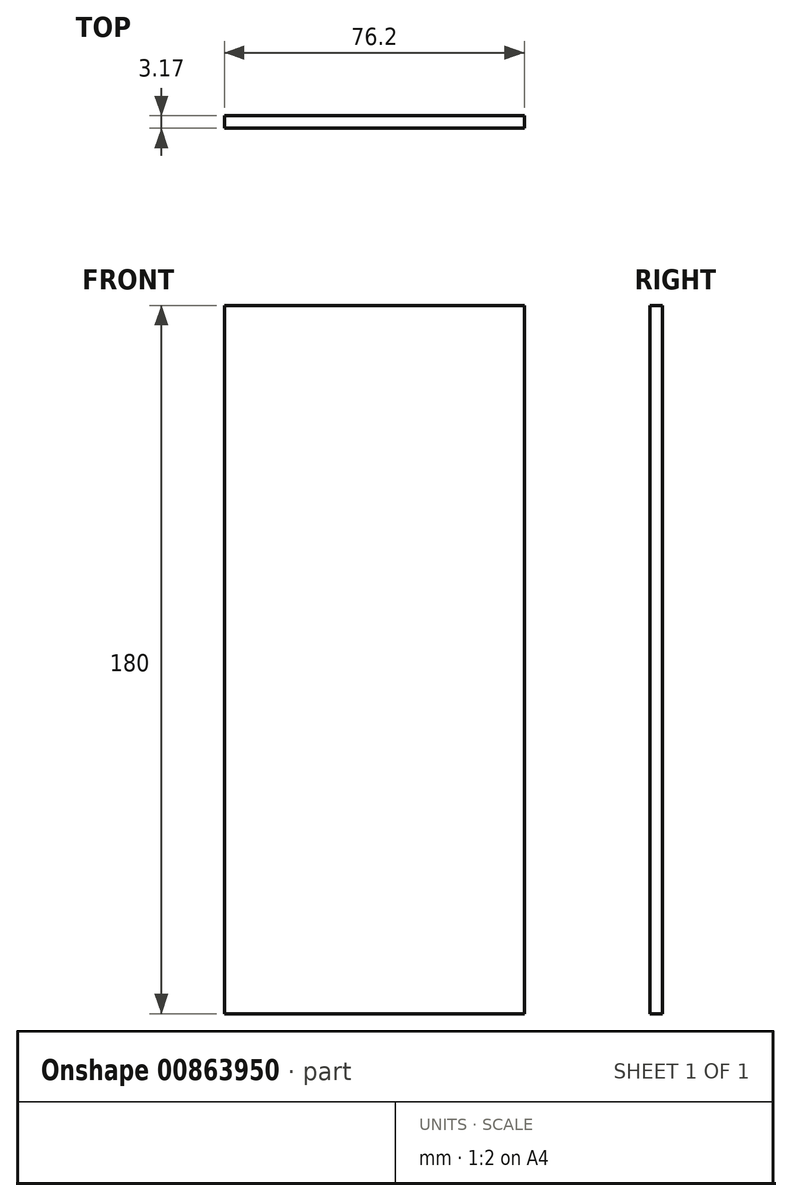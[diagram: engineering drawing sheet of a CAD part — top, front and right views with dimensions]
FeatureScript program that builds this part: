
annotation { "Feature Type Name" : "Feature", "Feature Type Description" : "" }
export const myFeature = defineFeature(function(context is Context, id is Id, definition is map)
    precondition{}
    {
        {
            var Q0;
            Q0=qCreatedBy(makeId("Front.planeOp"),FACE);
            var sketch = newSketch(context, id + "F0", { "sketchPlane" : qUnion([Q0])});
            skLineSegment(sketch, "E0.bottom", {"start": v(0, 0) * mm, "end": v(-76.2, 0) * mm});
            skLineSegment(sketch, "E0.top", {"start": v(0, -180) * mm, "end": v(-76.2, -180) * mm});
            skLineSegment(sketch, "E0.left", {"start": v(0, 0) * mm, "end": v(0, -180) * mm});
            skLineSegment(sketch, "E0.right", {"start": v(-76.2, 0) * mm, "end": v(-76.2, -180) * mm});
            skLineSegment(sketch, "E1.bottom", {"start": v(-24.24, 0) * mm, "end": v(-30.45, 0) * mm});
            skSolve(sketch);
        }
        {
            var Q0;
            Q0=makeQuery(id+"F0.imprint","IMPRINT",FACE,{"disambiguationData":[TD([[makeQuery(id+"F0.imprint","IMPRINT",EDGE,{"derivedFrom":sQuery(id+"F0.wireOp",EDGE,"E0.top")}),-1.0]])]});
            extrude(context, id + "F1", {"entities" : qUnion([Q0]), "depth" : 3.17 * mm, "offsetDistance" : 25.4 * mm});
        }
    });
